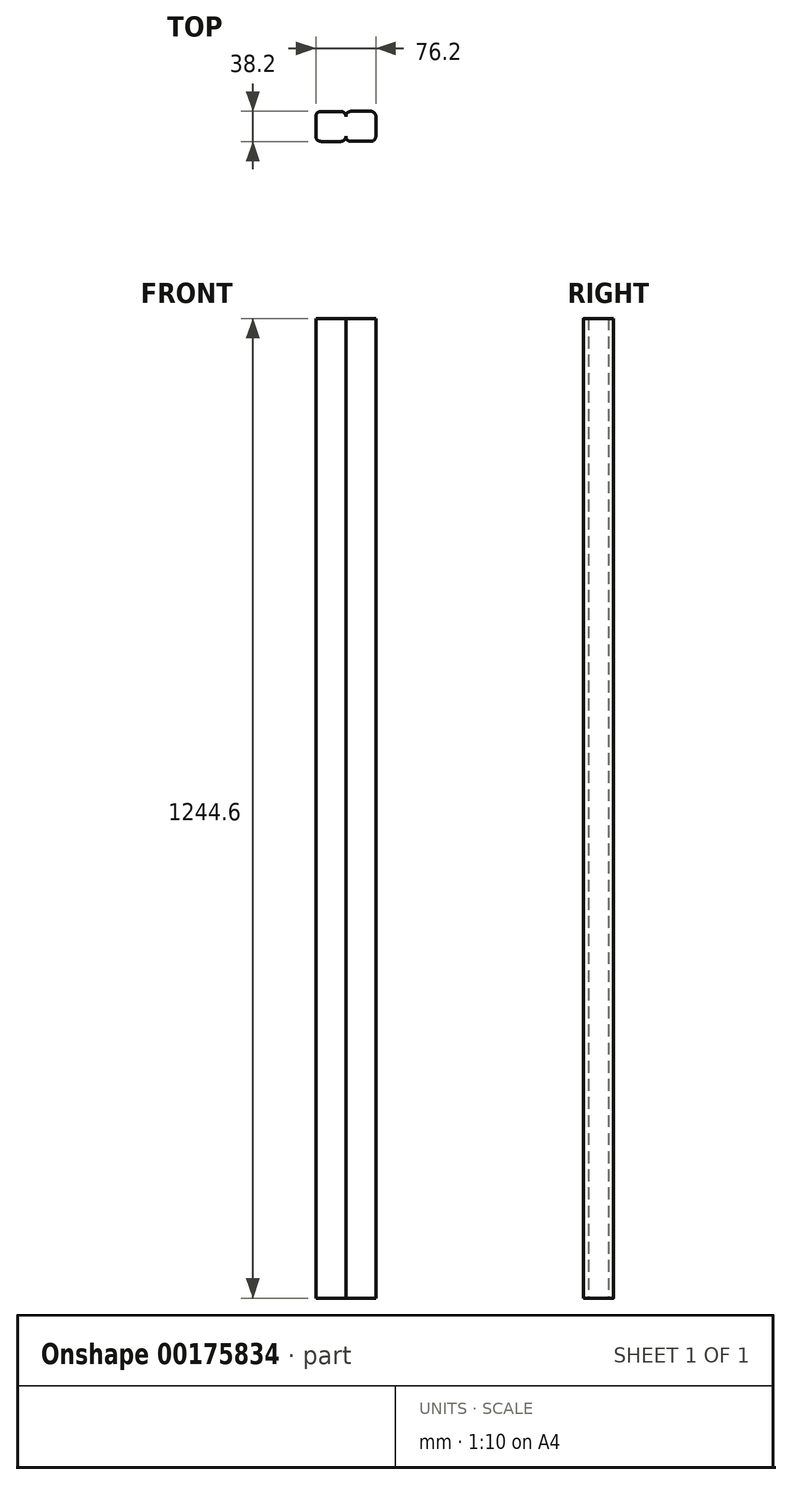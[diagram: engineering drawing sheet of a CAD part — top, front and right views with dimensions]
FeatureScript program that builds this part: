
annotation { "Feature Type Name" : "Feature", "Feature Type Description" : "" }
export const myFeature = defineFeature(function(context is Context, id is Id, definition is map)
    precondition{}
    {
        {
            var Q0;
            Q0=qCreatedBy(makeId("Top.planeOp"),FACE);
            var sketch = newSketch(context, id + "F0", { "sketchPlane" : qUnion([Q0])});
            skLineSegment(sketch, "E0.bottom", {"start": v(-6.35, 18.95) * mm, "end": v(-31.75, 18.95) * mm});
            skLineSegment(sketch, "E0.top", {"start": v(-6.35, -19.15) * mm, "end": v(-31.75, -19.15) * mm});
            skLineSegment(sketch, "E0.left", {"start": v(0, 12.6) * mm, "end": v(0, -12.8) * mm});
            skLineSegment(sketch, "E0.right", {"start": v(-38.1, 12.6) * mm, "end": v(-38.1, -12.8) * mm});
            skPoint(sketch, "E0.middle", {"position": v(-19.05, -0.1) * mm});
            skPoint(sketch, "E1.visualSharp", {"position": v(-38.1, 18.95) * mm});
            skArc(sketch, "E1.filletArc", {"start": v(-31.75, 18.95) * mm, "mid": v(-36.24, 17.09) * mm, "end": v(-38.1, 12.6) * mm});
            skPoint(sketch, "E2.visualSharp", {"position": v(0, 18.95) * mm});
            skArc(sketch, "E2.filletArc", {"start": v(0, 12.6) * mm, "mid": v(-1.86, 17.09) * mm, "end": v(-6.35, 18.95) * mm});
            skPoint(sketch, "E3.visualSharp", {"position": v(0, -19.15) * mm});
            skArc(sketch, "E3.filletArc", {"start": v(-6.35, -19.15) * mm, "mid": v(-1.86, -17.3) * mm, "end": v(0, -12.8) * mm});
            skPoint(sketch, "E4.visualSharp", {"position": v(-38.1, -19.15) * mm});
            skArc(sketch, "E4.filletArc", {"start": v(-38.1, -12.8) * mm, "mid": v(-36.24, -17.3) * mm, "end": v(-31.75, -19.15) * mm});
            skLineSegment(sketch, "E5.bottom", {"start": v(31.75, 19.05) * mm, "end": v(6.35, 19.05) * mm});
            skLineSegment(sketch, "E5.top", {"start": v(31.75, -19.05) * mm, "end": v(6.35, -19.05) * mm});
            skLineSegment(sketch, "E5.left", {"start": v(38.1, 12.7) * mm, "end": v(38.1, -12.7) * mm});
            skLineSegment(sketch, "E5.right", {"start": v(0, 12.7) * mm, "end": v(0, -12.7) * mm});
            skPoint(sketch, "E5.middle", {"position": v(19.05, 0) * mm});
            skPoint(sketch, "E6.visualSharp", {"position": v(0, 19.05) * mm});
            skArc(sketch, "E6.filletArc", {"start": v(6.35, 19.05) * mm, "mid": v(1.86, 17.2) * mm, "end": v(0, 12.7) * mm});
            skPoint(sketch, "E7.visualSharp", {"position": v(38.1, 19.05) * mm});
            skArc(sketch, "E7.filletArc", {"start": v(38.1, 12.7) * mm, "mid": v(36.24, 17.2) * mm, "end": v(31.75, 19.05) * mm});
            skPoint(sketch, "E8.visualSharp", {"position": v(38.1, -19.05) * mm});
            skArc(sketch, "E8.filletArc", {"start": v(31.75, -19.05) * mm, "mid": v(36.24, -17.2) * mm, "end": v(38.1, -12.7) * mm});
            skPoint(sketch, "E9.visualSharp", {"position": v(0, -19.05) * mm});
            skArc(sketch, "E9.filletArc", {"start": v(0, -12.7) * mm, "mid": v(1.86, -17.2) * mm, "end": v(6.35, -19.05) * mm});
            skSolve(sketch);
        }
        {
            var Q0;
            Q0=qSketchRegion(id+"F0",true);
            extrude(context, id + "F1", {"entities" : qUnion([Q0]), "depth" : 1244.6 * mm, "offsetDistance" : 25.4 * mm});
        }
    });
